FCSTD DOCUMENT  (FreeCAD 0.15R4671 (Git))
Label: weapon
License: All rights reserved
LicenseURL: http://en.wikipedia.org/wiki/All_rights_reserved
objects: Sketcher::SketchObject×1
note: 1 computed .brp shape members not serialized (recipe doc carries the construction recipe); baked Part::Feature solids carry a one-line shape summary decoded from their .brp

FEATURE [Sketcher::SketchObject] Sketch
  sketch-geometry (8):
    g0: LineSegment StartX=-95.1758 StartY=-0.0247762 StartZ=0 EndX=-46.0562 EndY=-0.0247762 EndZ=0
    g1: LineSegment StartX=47.8053 StartY=-0.0235374 StartZ=0 EndX=96.7296 EndY=-0.0235374 EndZ=0
    g2: ArcOfCircle CenterX=25.3367 CenterY=3.71636 CenterZ=0 NormalX=0 NormalY=0 NormalZ=1 Radius=71.4908 StartAngle=6.23085 EndAngle=9.47713
    g3: ArcOfCircle CenterX=-23.6853 CenterY=-0.234829 CenterZ=0 NormalX=0 NormalY=0 NormalZ=1 Radius=71.4908 StartAngle=3.13865 EndAngle=6.28614
    g4: LineSegment StartX=-23.0778 StartY=19.0516 StartZ=0 EndX=73.7512 EndY=19.0516 EndZ=0
    g5: ArcOfCircle CenterX=25.3367 CenterY=3.71636 CenterZ=0 NormalX=0 NormalY=0 NormalZ=1 Radius=50.7852 StartAngle=0.30675 EndAngle=2.83484
    g6: ArcOfCircle CenterX=-26.5493 CenterY=-3.71235 CenterZ=0 NormalX=0 NormalY=0 NormalZ=1 Radius=50.7852 StartAngle=3.44834 EndAngle=5.97644
    g7: LineSegment StartX=-74.9638 StartY=-19.0475 StartZ=0 EndX=21.8652 EndY=-19.0475 EndZ=0
  constraints (16):
    c: Coincident(g3,g1)
    c: Coincident(g2,g0)
    c: Coincident(g5,g2)
    c: Coincident(g4,g5)
    c: Coincident(g4,g5)
    c: Coincident(g7,g6)
    c: Coincident(g7,g6)
    c: Horizontal(g1)
    c: Horizontal(g0)
    c: Horizontal(g4)
    c: Horizontal(g7)
    c: Coincident(g3,g0)
    c: Coincident(g1,g2)
    c: Equal(g4,g7)
    c: Equal(g6,g5)
    c: Equal(g2,g3)
